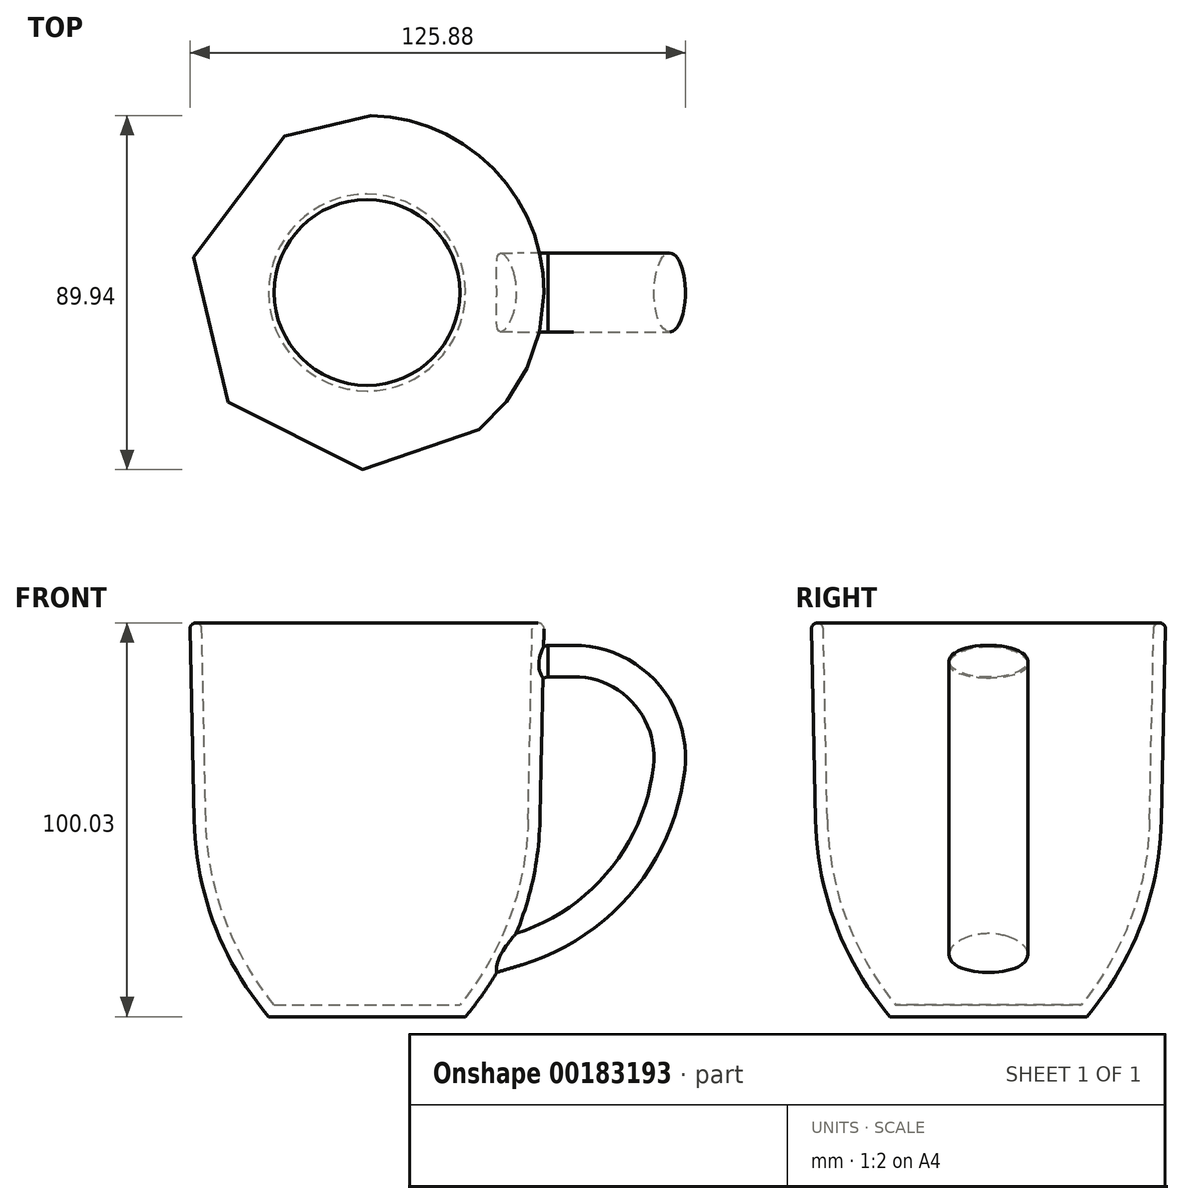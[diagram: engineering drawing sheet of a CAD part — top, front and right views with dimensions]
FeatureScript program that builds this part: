
annotation { "Feature Type Name" : "Feature", "Feature Type Description" : "" }
export const myFeature = defineFeature(function(context is Context, id is Id, definition is map)
    precondition{}
    {
        {
            var Q0;
            Q0=qCreatedBy(makeId("Front.planeOp"),FACE);
            var sketch = newSketch(context, id + "F0", { "sketchPlane" : qUnion([Q0])});
            skLineSegment(sketch, "E0", {"start": v(0, 0) * mm, "end": v(0, 110.58) * mm, "construction": true});
            skArc(sketch, "E1", {"start": v(25, 0) * mm, "mid": v(38.77, 23.38) * mm, "end": v(43.94, 50.01) * mm});
            skLineSegment(sketch, "E2", {"start": v(25, 0) * mm, "end": v(0, 0) * mm});
            skLineSegment(sketch, "E3", {"start": v(43.94, 50.01) * mm, "end": v(45, 100) * mm});
            skLineSegment(sketch, "E4.0", {"start": v(40.94, 50.07) * mm, "end": v(42, 100.06) * mm});
            skArc(sketch, "E4.1", {"start": v(23.6, 3) * mm, "mid": v(36.2, 25.09) * mm, "end": v(40.94, 50.07) * mm});
            skLineSegment(sketch, "E4.2", {"start": v(23.6, 3) * mm, "end": v(0, 3) * mm});
            skLineSegment(sketch, "E5", {"start": v(0, 0) * mm, "end": v(0, 3) * mm});
            skLineSegment(sketch, "E6", {"start": v(42, 100.06) * mm, "end": v(45, 100) * mm});
            skSolve(sketch);
        }
        {
            var Q0;
            Q0=makeQuery(id+"F0.imprint","IMPRINT",FACE,{"disambiguationData":[TD([[makeQuery(id+"F0.imprint","IMPRINT",EDGE,{"derivedFrom":sQuery(id+"F0.wireOp",EDGE,"E1")}),1.0]])]});
            var Q1;
            Q1=sQuery(id+"F0.wireOp",EDGE,"E3");
            var Q2;
            Q2=sQuery(id+"F0.wireOp",EDGE,"E1");
            var Q3;
            Q3=sQuery(id+"F0.wireOp",EDGE,"E2");
            var Q4;
            Q4=sQuery(id+"F0.wireOp",EDGE,"E0");
            revolve(context, id + "F1", {"entities" : qUnion([Q0]), "surfaceEntities" : qUnion([Q1, Q2, Q3]), "axis" : qUnion([Q4]), "revolveType" : RevolveType.FULL});
        }
        {
            var Q0;
            Q0=makeQuery(id+"F1.opRevolve","SWEPT_EDGE",EDGE,{"disambiguationData":[OSD([sQuery(id+"F0.wireOp",EDGE,"E4.0"),sQuery(id+"F0.wireOp",EDGE,"E6")])]});
            var Q1;
            Q1=makeQuery(id+"F1.opRevolve","SWEPT_EDGE",EDGE,{"disambiguationData":[OSD([sQuery(id+"F0.wireOp",EDGE,"E3"),sQuery(id+"F0.wireOp",EDGE,"E6")])]});
            fillet(context, id + "F2", {"entities" : qUnion([Q0, Q1]), "radius" : 1.5 * mm, "tangentPropagation" : true, "allowEdgeOverflow" : false});
        }
        {
            var Q0;
            Q0=qCreatedBy(makeId("Front.planeOp"),FACE);
            var sketch = newSketch(context, id + "F3", { "sketchPlane" : qUnion([Q0])});
            skLineSegment(sketch, "E7", {"start": v(45.98, 90.37) * mm, "end": v(52.47, 90.37) * mm});
            skArc(sketch, "E8", {"start": v(52.47, 90.37) * mm, "mid": v(70.72, 82.19) * mm, "end": v(76.75, 63.12) * mm});
            skArc(sketch, "E9", {"start": v(76.75, 63.12) * mm, "mid": v(64.4, 34.33) * mm, "end": v(38.28, 17.04) * mm});
            skSolve(sketch);
        }
        {
            var Q0;
            Q0=sQuery(id+"F3.wireOp",VERTEX,"E7.start");
            var Q1;
            Q1=sQuery(id+"F3.wireOp",EDGE,"E7");
            cPlane(context, id + "F4", {"entities" : qUnion([Q0, Q1]), "cplaneType" : CPlaneType.LINE_POINT, "offset" : 25 * mm, "width" : 150 * mm, "height" : 150 * mm});
        }
        {
            var Q0;
            Q0=qCreatedBy(id+"F4.planeOp",FACE);
            var sketch = newSketch(context, id + "F5", { "sketchPlane" : qUnion([Q0])});
            skEllipse(sketch, "E10", {"center": v(0, 90.37) * mm, "majorRadius": 10 * mm, "minorRadius": 4 * mm, "majorAxis": v(1, 0)});
            skSolve(sketch);
        }
        {
            var Q0;
            Q0=makeQuery(id+"F5.imprint","IMPRINT",FACE,{"disambiguationData":[TD([[makeQuery(id+"F5.imprint","IMPRINT",EDGE,{"derivedFrom":sQuery(id+"F5.wireOp",EDGE,"E10")}),1.0]])]});
            var Q1;
            Q1=sQuery(id+"F3.wireOp",EDGE,"E7");
            var Q2;
            Q2=sQuery(id+"F3.wireOp",EDGE,"E8");
            var Q3;
            Q3=sQuery(id+"F3.wireOp",EDGE,"E9");
            sweep(context, id + "F6", {"operationType" : NewBodyOperationType.ADD, "profiles" : qUnion([Q0]), "path" : qUnion([Q1, Q2, Q3])});
        }
        {
            var Q0;
            Q0=makeQuery(id+"F6.opSweep","CAP_FACE",FACE,{"disambiguationData":[OSD([sQuery(id+"F3.wireOp",VERTEX,"E9.end"),sQuery(id+"F5.wireOp",EDGE,"E10")])],"isStart":false});
            var Q1;
            Q1=makeQuery(id+"F6.boolean.opBoolean","SPLIT",FACE,{"disambiguationData":[OD(0.0)],"derivedFrom":makeQuery(id+"F6.opSweep","CAP_FACE",FACE,{"disambiguationData":[OSD([sQuery(id+"F3.wireOp",VERTEX,"E7.start"),sQuery(id+"F5.wireOp",EDGE,"E10")])],"isStart":true})});
            var Q2;
            Q2=makeQuery(id+"F6.boolean.opBoolean","SPLIT",FACE,{"disambiguationData":[OD(1.0)],"derivedFrom":makeQuery(id+"F6.opSweep","CAP_FACE",FACE,{"disambiguationData":[OSD([sQuery(id+"F3.wireOp",VERTEX,"E7.start"),sQuery(id+"F5.wireOp",EDGE,"E10")])],"isStart":true})});
            extrude(context, id + "F7", {"entities" : qUnion([Q0, Q1, Q2]), "operationType" : NewBodyOperationType.ADD, "endBound" : BoundingType.UP_TO_NEXT, "depth" : 25 * mm});
        }
    });
